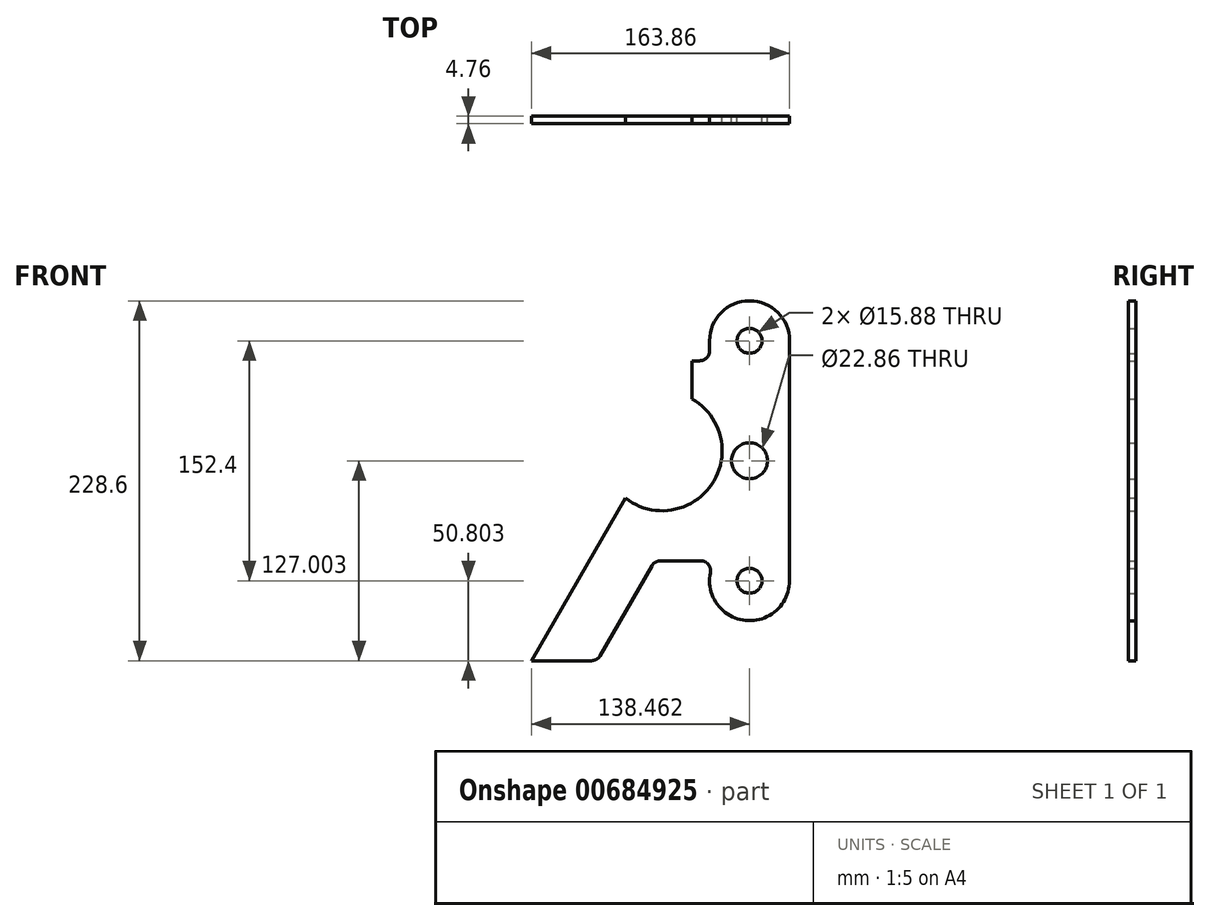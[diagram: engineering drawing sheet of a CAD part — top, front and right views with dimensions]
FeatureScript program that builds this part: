
annotation { "Feature Type Name" : "Feature", "Feature Type Description" : "" }
export const myFeature = defineFeature(function(context is Context, id is Id, definition is map)
    precondition{}
    {
        {
            var Q0;
            Q0=qCreatedBy(makeId("Front.planeOp"),FACE);
            var sketch = newSketch(context, id + "F0", { "sketchPlane" : qUnion([Q0])});
            skLineSegment(sketch, "E0", {"start": v(42.35, 87.26) * mm, "end": v(47.11, 87.26) * mm});
            skLineSegment(sketch, "E1", {"start": v(53.46, 93.61) * mm, "end": v(53.46, 99.96) * mm});
            skLineSegment(sketch, "E2", {"start": v(104.26, 99.96) * mm, "end": v(104.26, -52.44) * mm});
            skLineSegment(sketch, "E3", {"start": v(42.35, 87.26) * mm, "end": v(42.35, 63.13) * mm});
            skArc(sketch, "E4", {"start": v(42.35, 63.13) * mm, "mid": v(54.98, 8.89) * mm, "end": v(0, 0) * mm});
            skArc(sketch, "E5", {"start": v(53.46, 99.96) * mm, "mid": v(78.86, 125.36) * mm, "end": v(104.26, 99.96) * mm});
            skCircle(sketch, "E6", {"center": v(78.86, 99.96) * mm, "radius": 7.94 * mm});
            skArc(sketch, "E7.MirrorCS", {"start": v(53.98, -47.36) * mm, "mid": v(76.3, -77.7) * mm, "end": v(104.26, -52.44) * mm});
            skCircle(sketch, "E8.MirrorC", {"center": v(78.86, -52.44) * mm, "radius": 7.94 * mm});
            skLineSegment(sketch, "E9", {"start": v(47.75, -39.74) * mm, "end": v(22.43, -39.74) * mm});
            skLineSegment(sketch, "E10", {"start": v(16.93, -42.91) * mm, "end": v(-16.06, -100.06) * mm});
            skPoint(sketch, "E11.visualSharp", {"position": v(53.46, 87.26) * mm});
            skArc(sketch, "E11.filletArc", {"start": v(47.11, 87.26) * mm, "mid": v(51.6, 89.12) * mm, "end": v(53.46, 93.61) * mm});
            skPoint(sketch, "E12.visualSharp", {"position": v(56.87, -39.74) * mm});
            skArc(sketch, "E12.filletArc", {"start": v(53.98, -47.36) * mm, "mid": v(52.67, -42.07) * mm, "end": v(47.75, -39.74) * mm});
            skPoint(sketch, "E13.visualSharp", {"position": v(18.77, -39.74) * mm});
            skArc(sketch, "E13.filletArc", {"start": v(22.43, -39.74) * mm, "mid": v(19.26, -40.59) * mm, "end": v(16.93, -42.91) * mm});
            skLineSegment(sketch, "E14", {"start": v(0, 0) * mm, "end": v(-59.6, -103.24) * mm});
            skLineSegment(sketch, "E15", {"start": v(-59.6, -103.24) * mm, "end": v(-21.56, -103.24) * mm});
            skLineSegment(sketch, "E16", {"start": v(78.86, 125.36) * mm, "end": v(78.86, -77.84) * mm, "construction": true});
            skPoint(sketch, "E16.startSnap0", {"position": v(78.86, 125.36) * mm});
            skLineSegment(sketch, "E17", {"start": v(0, 0) * mm, "end": v(42.35, 63.13) * mm, "construction": true});
            skLineSegment(sketch, "E18", {"start": v(-87.11, 0) * mm, "end": v(123.45, 0) * mm, "construction": true});
            skPoint(sketch, "E19.visualSharp", {"position": v(-17.9, -103.24) * mm});
            skArc(sketch, "E19.filletArc", {"start": v(-21.56, -103.24) * mm, "mid": v(-18.39, -102.39) * mm, "end": v(-16.06, -100.06) * mm});
            skCircle(sketch, "E20", {"center": v(78.86, 23.76) * mm, "radius": 11.43 * mm});
            skSolve(sketch);
        }
        {
            var Q0;
            Q0 = qSketchRegion(id + "F0", true);
            extrude(context, id + "F1", {"entities" : qUnion([Q0]), "depth" : 4.76 * mm, "offsetDistance" : 25.4 * mm});
        }
    });
